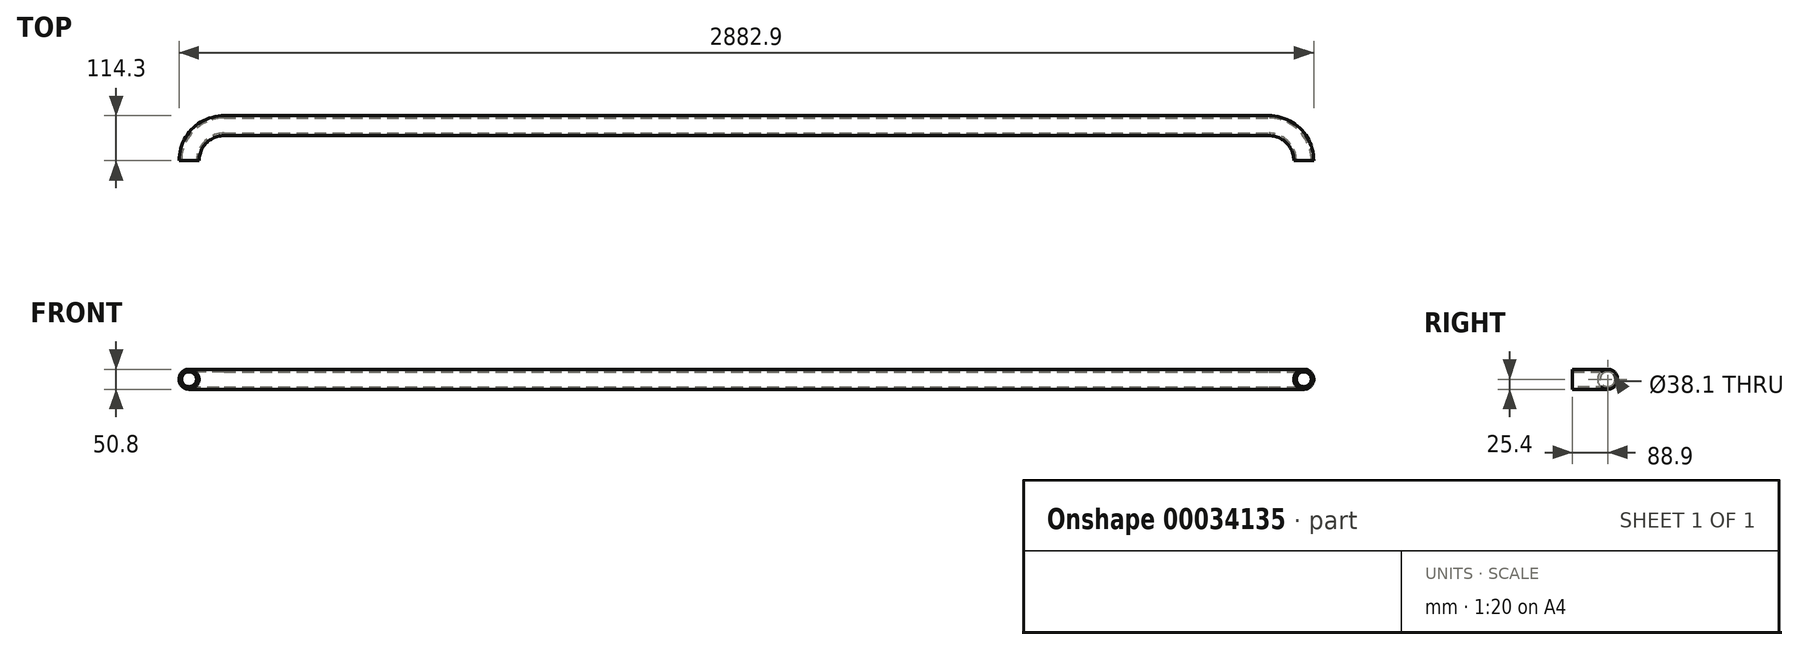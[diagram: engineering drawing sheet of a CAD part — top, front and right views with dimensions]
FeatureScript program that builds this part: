
annotation { "Feature Type Name" : "Feature", "Feature Type Description" : "" }
export const myFeature = defineFeature(function(context is Context, id is Id, definition is map)
    precondition{}
    {
        {
            var Q0;
            Q0=qCreatedBy(makeId("Front.planeOp"),FACE);
            var sketch = newSketch(context, id + "F0", { "sketchPlane" : qUnion([Q0])});
            skCircle(sketch, "E0", {"center": v(0, 0) * mm, "radius": 25.4 * mm});
            skCircle(sketch, "E1", {"center": v(0, 0) * mm, "radius": 19.05 * mm});
            skSolve(sketch);
        }
        {
            var Q0;
            Q0=qCreatedBy(makeId("Top.planeOp"),FACE);
            var sketch = newSketch(context, id + "F1", { "sketchPlane" : qUnion([Q0])});
            skLineSegment(sketch, "E2", {"start": v(0, 0) * mm, "end": v(0, 0) * mm});
            skLineSegment(sketch, "E3", {"start": v(88.9, 88.9) * mm, "end": v(2743.2, 88.9) * mm});
            skLineSegment(sketch, "E4", {"start": v(2832.1, 0) * mm, "end": v(2832.1, 0) * mm});
            skPoint(sketch, "E5.visualSharp", {"position": v(0, 88.9) * mm});
            skArc(sketch, "E5.filletArc", {"start": v(88.9, 88.9) * mm, "mid": v(26.04, 62.86) * mm, "end": v(0, 0) * mm});
            skPoint(sketch, "E6.visualSharp", {"position": v(2832.1, 88.9) * mm});
            skArc(sketch, "E6.filletArc", {"start": v(2832.1, 0) * mm, "mid": v(2806.06, 62.86) * mm, "end": v(2743.2, 88.9) * mm});
            skPoint(sketch, "E7.visualSharp", {"position": v(2832.1, 0) * mm});
            skPoint(sketch, "E8.start.orphan", {"position": v(1219.2, 0) * mm});
            skSolve(sketch);
        }
        {
            var Q0;
            Q0=makeQuery(id+"F0.imprint","IMPRINT",FACE,{"disambiguationData":[TD([[makeQuery(id+"F0.imprint","IMPRINT",EDGE,{"derivedFrom":sQuery(id+"F0.wireOp",EDGE,"E0")}),1.0]])]});
            var Q1;
            Q1=sQuery(id+"F1.wireOp",EDGE,"E2");
            var Q2;
            Q2=sQuery(id+"F1.wireOp",EDGE,"E5.filletArc");
            var Q3;
            Q3=sQuery(id+"F1.wireOp",EDGE,"E3");
            var Q4;
            Q4=sQuery(id+"F1.wireOp",EDGE,"E6.filletArc");
            var Q5;
            Q5=sQuery(id+"F1.wireOp",EDGE,"E4");
            sweep(context, id + "F2", {"profiles" : qUnion([Q0]), "path" : qUnion([Q1, Q2, Q3, Q4, Q5])});
        }
    });
